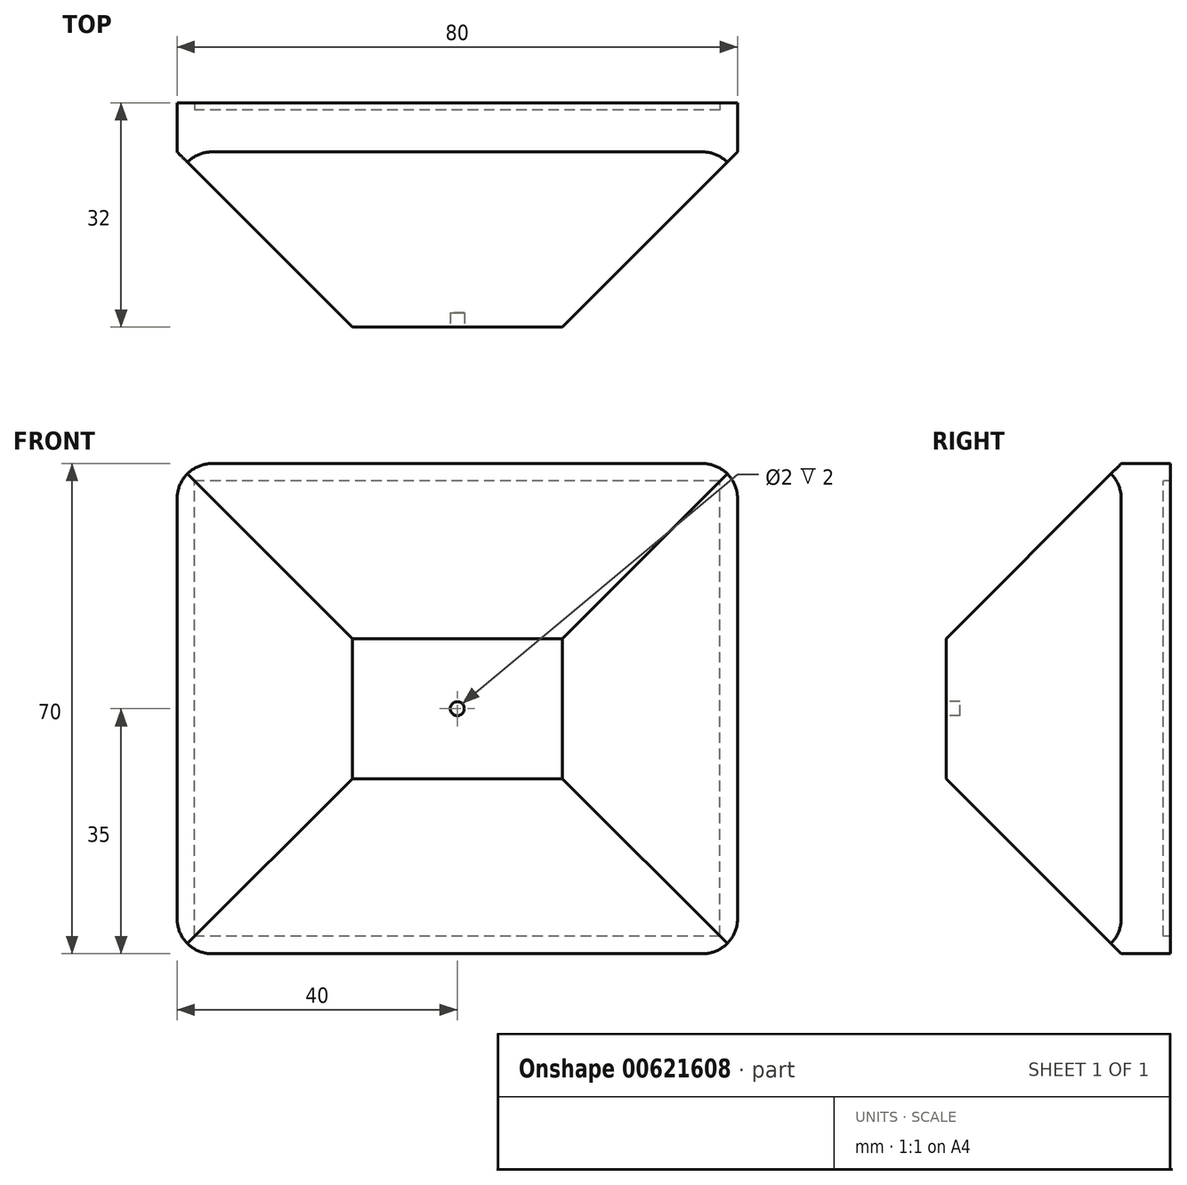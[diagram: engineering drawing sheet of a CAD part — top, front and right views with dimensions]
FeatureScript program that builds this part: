
annotation { "Feature Type Name" : "Feature", "Feature Type Description" : "" }
export const myFeature = defineFeature(function(context is Context, id is Id, definition is map)
    precondition{}
    {
        {
            var Q0;
            Q0=qCreatedBy(makeId("Front.planeOp"),FACE);
            var sketch = newSketch(context, id + "F0", { "sketchPlane" : qUnion([Q0])});
            skLineSegment(sketch, "E0.bottom", {"start": v(40, -35) * mm, "end": v(-40, -35) * mm});
            skLineSegment(sketch, "E0.top", {"start": v(40, 35) * mm, "end": v(-40, 35) * mm});
            skLineSegment(sketch, "E0.left", {"start": v(40, -35) * mm, "end": v(40, 35) * mm});
            skLineSegment(sketch, "E0.right", {"start": v(-40, -35) * mm, "end": v(-40, 35) * mm});
            skPoint(sketch, "E0.middle", {"position": v(0, 0) * mm});
            skSolve(sketch);
        }
        {
            var Q0;
            Q0=makeQuery(id+"F0.imprint","IMPRINT",FACE,{"disambiguationData":[TD([[makeQuery(id+"F0.imprint","IMPRINT",EDGE,{"derivedFrom":sQuery(id+"F0.wireOp",EDGE,"E0.bottom")}),-1.0]])]});
            extrude(context, id + "F1", {"entities" : qUnion([Q0]), "depth" : 26 * mm, "offsetDistance" : 25 * mm});
        }
        {
            var Q0;
            Q0=makeQuery(id+"F1.opExtrude","CAP_FACE",FACE,{"disambiguationData":[OSD([sQuery(id+"F0.wireOp",EDGE,"E0.bottom"),sQuery(id+"F0.wireOp",EDGE,"E0.top"),sQuery(id+"F0.wireOp",EDGE,"E0.left"),sQuery(id+"F0.wireOp",EDGE,"E0.right")])],"isStart":false});
            chamfer(context, id + "F2", {"entities" : qUnion([Q0]), "width" : 25 * mm, "tangentPropagation" : true});
        }
        {
            var Q0;
            Q0=makeQuery(id+"F1.opExtrude","CAP_FACE",FACE,{"disambiguationData":[OSD([sQuery(id+"F0.wireOp",EDGE,"E0.bottom"),sQuery(id+"F0.wireOp",EDGE,"E0.top"),sQuery(id+"F0.wireOp",EDGE,"E0.left"),sQuery(id+"F0.wireOp",EDGE,"E0.right")])],"isStart":true});
            extrude(context, id + "F3", {"entities" : qUnion([Q0]), "operationType" : NewBodyOperationType.ADD, "depth" : 5 * mm, "offsetDistance" : 25 * mm});
        }
        {
            var Q0;
            {var subQ0=sQuery(id+"F0.wireOp",EDGE,"E0.left");var subQ1=sQuery(id+"F0.wireOp",EDGE,"E0.top");Q0=makeQuery(id+"F3.boolean.opBoolean","MERGE",EDGE,{"derivedFrom":[makeQuery(id+"F1.opExtrude","SWEPT_EDGE",EDGE,{"disambiguationData":[OSD([subQ1,subQ0])]}),makeQuery(id+"F3.opExtrude","SWEPT_EDGE",EDGE,{"disambiguationData":[OSD([subQ1,subQ0])]})]});}
            var Q1;
            {var subQ0=sQuery(id+"F0.wireOp",EDGE,"E0.right");var subQ1=sQuery(id+"F0.wireOp",EDGE,"E0.top");Q1=makeQuery(id+"F3.boolean.opBoolean","MERGE",EDGE,{"derivedFrom":[makeQuery(id+"F1.opExtrude","SWEPT_EDGE",EDGE,{"disambiguationData":[OSD([subQ1,subQ0])]}),makeQuery(id+"F3.opExtrude","SWEPT_EDGE",EDGE,{"disambiguationData":[OSD([subQ1,subQ0])]})]});}
            var Q2;
            {var subQ0=sQuery(id+"F0.wireOp",EDGE,"E0.left");var subQ1=sQuery(id+"F0.wireOp",EDGE,"E0.bottom");Q2=makeQuery(id+"F3.boolean.opBoolean","MERGE",EDGE,{"derivedFrom":[makeQuery(id+"F1.opExtrude","SWEPT_EDGE",EDGE,{"disambiguationData":[OSD([subQ1,subQ0])]}),makeQuery(id+"F3.opExtrude","SWEPT_EDGE",EDGE,{"disambiguationData":[OSD([subQ1,subQ0])]})]});}
            var Q3;
            {var subQ0=sQuery(id+"F0.wireOp",EDGE,"E0.right");var subQ1=sQuery(id+"F0.wireOp",EDGE,"E0.bottom");Q3=makeQuery(id+"F3.boolean.opBoolean","MERGE",EDGE,{"derivedFrom":[makeQuery(id+"F1.opExtrude","SWEPT_EDGE",EDGE,{"disambiguationData":[OSD([subQ1,subQ0])]}),makeQuery(id+"F3.opExtrude","SWEPT_EDGE",EDGE,{"disambiguationData":[OSD([subQ1,subQ0])]})]});}
            fillet(context, id + "F4", {"entities" : qUnion([Q0, Q1, Q2, Q3]), "radius" : 5 * mm, "tangentPropagation" : true, "allowEdgeOverflow" : false});
        }
        {
            var Q0;
            Q0=makeQuery(id+"F3.opExtrude","CAP_FACE",FACE,{"disambiguationData":[OSD([sQuery(id+"F0.wireOp",EDGE,"E0.bottom"),sQuery(id+"F0.wireOp",EDGE,"E0.top"),sQuery(id+"F0.wireOp",EDGE,"E0.left"),sQuery(id+"F0.wireOp",EDGE,"E0.right")])],"isStart":false});
            var sketch = newSketch(context, id + "F5", { "sketchPlane" : qUnion([Q0])});
            skLineSegment(sketch, "E1.bottom", {"start": v(-37.5, -32.5) * mm, "end": v(37.5, -32.5) * mm});
            skLineSegment(sketch, "E1.top", {"start": v(-37.5, 32.5) * mm, "end": v(37.5, 32.5) * mm});
            skLineSegment(sketch, "E1.left", {"start": v(-37.5, -32.5) * mm, "end": v(-37.5, 32.5) * mm});
            skLineSegment(sketch, "E1.right", {"start": v(37.5, -32.5) * mm, "end": v(37.5, 32.5) * mm});
            skPoint(sketch, "E1.middle", {"position": v(0, 0) * mm});
            skSolve(sketch);
        }
        {
            var Q0;
            Q0=makeQuery(id+"F5.imprint","IMPRINT",FACE,{"disambiguationData":[TD([[makeQuery(id+"F5.imprint","IMPRINT",EDGE,{"derivedFrom":sQuery(id+"F5.wireOp",EDGE,"E1.bottom")}),-1.0]])]});
            extrude(context, id + "F6", {"entities" : qUnion([Q0]), "operationType" : NewBodyOperationType.ADD, "depth" : 1 * mm, "offsetDistance" : 25 * mm});
        }
        {
            var Q0;
            Q0=makeQuery(id+"F1.opExtrude","CAP_FACE",FACE,{"disambiguationData":[OSD([sQuery(id+"F0.wireOp",EDGE,"E0.bottom"),sQuery(id+"F0.wireOp",EDGE,"E0.top"),sQuery(id+"F0.wireOp",EDGE,"E0.left"),sQuery(id+"F0.wireOp",EDGE,"E0.right")])],"isStart":false});
            var sketch = newSketch(context, id + "F7", { "sketchPlane" : qUnion([Q0])});
            skCircle(sketch, "E2", {"center": v(0, 0) * mm, "radius": 1 * mm});
            skSolve(sketch);
        }
        {
            var Q0;
            Q0=makeQuery(id+"F7.imprint","IMPRINT",FACE,{"disambiguationData":[TD([[makeQuery(id+"F7.imprint","IMPRINT",EDGE,{"derivedFrom":sQuery(id+"F7.wireOp",EDGE,"E2")}),1.0]])]});
            extrude(context, id + "F8", {"entities" : qUnion([Q0]), "operationType" : NewBodyOperationType.REMOVE, "oppositeDirection" : true, "depth" : 2 * mm, "offsetDistance" : 25 * mm});
        }
    });
